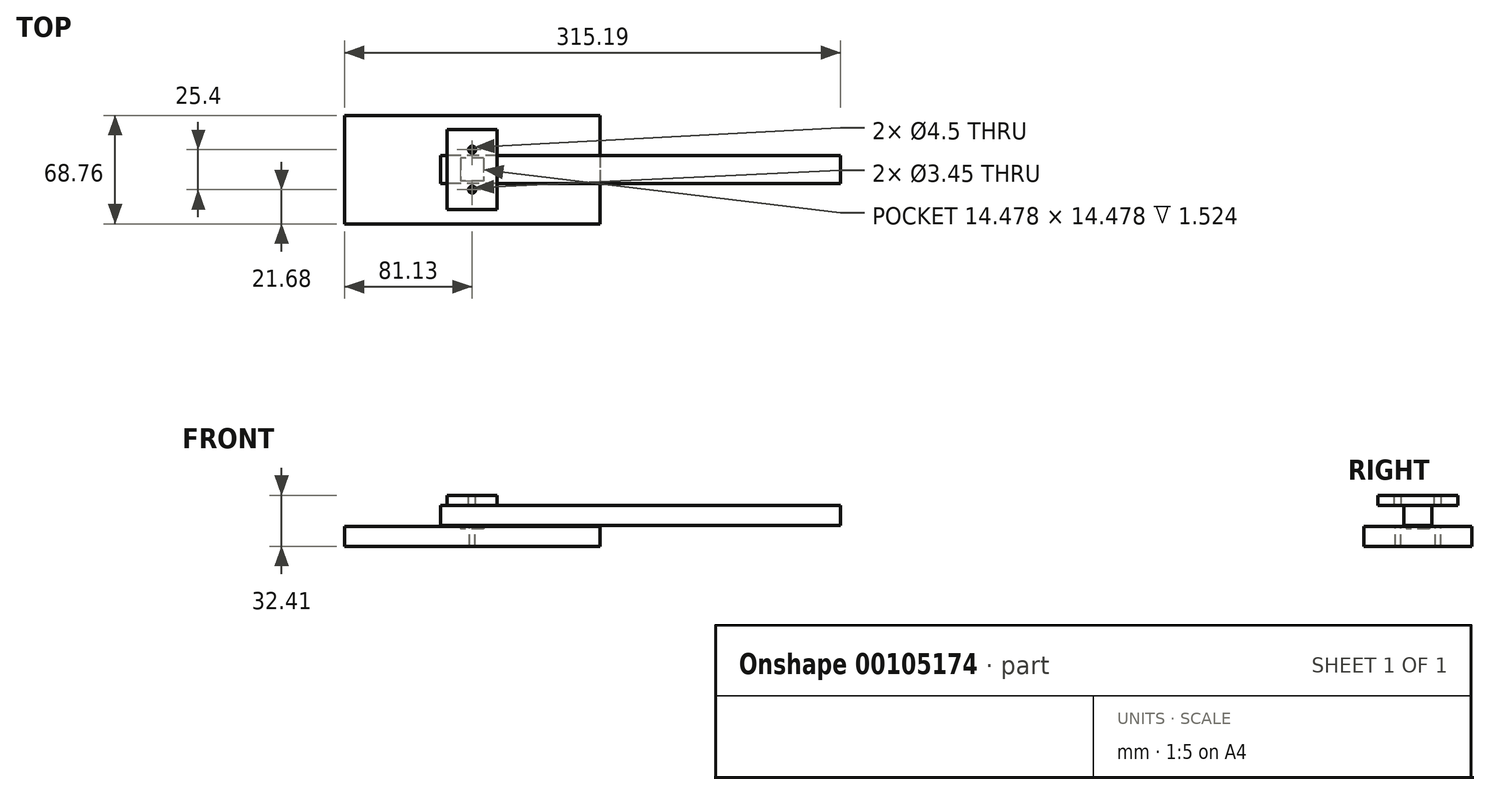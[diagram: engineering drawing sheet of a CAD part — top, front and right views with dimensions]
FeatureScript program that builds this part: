
annotation { "Feature Type Name" : "Feature", "Feature Type Description" : "" }
export const myFeature = defineFeature(function(context is Context, id is Id, definition is map)
    precondition{}
    {
        {
            var Q0;
            Q0=qCreatedBy(makeId("Top.planeOp"),FACE);
            var sketch = newSketch(context, id + "F0", { "sketchPlane" : qUnion([Q0])});
            skLineSegment(sketch, "E0.bottom", {"start": v(81.13, 34.38) * mm, "end": v(-81.13, 34.38) * mm});
            skLineSegment(sketch, "E0.top", {"start": v(81.13, -34.38) * mm, "end": v(-81.13, -34.38) * mm});
            skLineSegment(sketch, "E0.left", {"start": v(81.13, 34.38) * mm, "end": v(81.13, -34.38) * mm});
            skLineSegment(sketch, "E0.right", {"start": v(-81.13, 34.38) * mm, "end": v(-81.13, -34.38) * mm});
            skPoint(sketch, "E0.middle", {"position": v(0, 0) * mm});
            skSolve(sketch);
        }
        {
            var Q0;
            Q0=makeQuery(id+"F0.imprint","IMPRINT",FACE,{"disambiguationData":[TD([[makeQuery(id+"F0.imprint","IMPRINT",EDGE,{"derivedFrom":sQuery(id+"F0.wireOp",EDGE,"E0.bottom")}),1.0]])]});
            extrude(context, id + "F1", {"entities" : qUnion([Q0]), "depth" : 12.7 * mm});
        }
        {
            var Q0;
            Q0=makeQuery(id+"F1.opExtrude","CAP_FACE",FACE,{"disambiguationData":[OSD([sQuery(id+"F0.wireOp",EDGE,"E0.bottom"),sQuery(id+"F0.wireOp",EDGE,"E0.top"),sQuery(id+"F0.wireOp",EDGE,"E0.left"),sQuery(id+"F0.wireOp",EDGE,"E0.right")])],"isStart":false});
            var sketch = newSketch(context, id + "F2", { "sketchPlane" : qUnion([Q0])});
            skLineSegment(sketch, "E1.0.0", {"start": v(81.13, -34.38) * mm, "end": v(81.13, 34.38) * mm});
            skLineSegment(sketch, "E1.0.1", {"start": v(81.13, 34.38) * mm, "end": v(-81.13, 34.38) * mm});
            skLineSegment(sketch, "E1.0.2", {"start": v(-81.13, 34.38) * mm, "end": v(-81.13, -34.38) * mm});
            skLineSegment(sketch, "E1.0.3", {"start": v(-81.13, -34.38) * mm, "end": v(81.13, -34.38) * mm});
            skLineSegment(sketch, "E2", {"start": v(-81.13, 0) * mm, "end": v(81.13, 0) * mm, "construction": true});
            skLineSegment(sketch, "E3", {"start": v(0, 34.38) * mm, "end": v(0, -34.38) * mm, "construction": true});
            skLineSegment(sketch, "E4.bottom", {"start": v(7.24, 7.24) * mm, "end": v(-7.24, 7.24) * mm});
            skLineSegment(sketch, "E4.top", {"start": v(7.24, -7.24) * mm, "end": v(-7.24, -7.24) * mm});
            skLineSegment(sketch, "E4.left", {"start": v(7.24, 7.24) * mm, "end": v(7.24, -7.24) * mm});
            skLineSegment(sketch, "E4.right", {"start": v(-7.24, 7.24) * mm, "end": v(-7.24, -7.24) * mm});
            skPoint(sketch, "E4.middle", {"position": v(0, 0) * mm});
            skSolve(sketch);
        }
        {
            var Q0;
            Q0=makeQuery(id+"F2.imprint","IMPRINT",FACE,{"disambiguationData":[TD([[makeQuery(id+"F2.imprint","IMPRINT",EDGE,{"derivedFrom":sQuery(id+"F2.wireOp",EDGE,"E4.bottom")}),1.0]])]});
            extrude(context, id + "F3", {"entities" : qUnion([Q0]), "operationType" : NewBodyOperationType.REMOVE, "oppositeDirection" : true, "depth" : 1.52 * mm});
        }
        {
            var Q0;
            Q0=makeQuery(id+"F3.boolean.opBoolean","COPY",FACE,{"derivedFrom":makeQuery(id+"F3.opExtrude","CAP_FACE",FACE,{"disambiguationData":[OSD([sQuery(id+"F2.wireOp",EDGE,"E4.bottom"),sQuery(id+"F2.wireOp",EDGE,"E4.top"),sQuery(id+"F2.wireOp",EDGE,"E4.left"),sQuery(id+"F2.wireOp",EDGE,"E4.right")])],"isStart":false})});
            extrude(context, id + "F4", {"entities" : qUnion([Q0]), "depth" : 2.18 * mm});
        }
        {
            var Q0;
            Q0=makeQuery(id+"F4.opExtrude","SWEPT_FACE",FACE,{"disambiguationData":[OSD([sQuery(id+"F2.wireOp",EDGE,"E4.right")])]});
            cPlane(context, id + "F5", {"entities" : qUnion([Q0]), "cplaneType" : CPlaneType.OFFSET, "offset" : 12.7 * mm, "width" : 152.4 * mm, "height" : 152.4 * mm});
        }
        {
            var Q0;
            Q0=qCreatedBy(id+"F5.planeOp",FACE);
            var sketch = newSketch(context, id + "F6", { "sketchPlane" : qUnion([Q0])});
            skLineSegment(sketch, "E5.0.0", {"start": v(-7.24, 11.18) * mm, "end": v(7.24, 11.18) * mm});
            skLineSegment(sketch, "E5.0.1", {"start": v(7.24, 11.18) * mm, "end": v(7.24, 13.36) * mm});
            skLineSegment(sketch, "E5.0.2", {"start": v(7.24, 13.36) * mm, "end": v(-7.24, 13.36) * mm});
            skLineSegment(sketch, "E5.0.3", {"start": v(-7.24, 13.36) * mm, "end": v(-7.24, 11.18) * mm});
            skLineSegment(sketch, "E6.bottom", {"start": v(-8.9, 26.06) * mm, "end": v(8.89, 26.06) * mm});
            skLineSegment(sketch, "E6.top", {"start": v(-8.9, 13.36) * mm, "end": v(8.89, 13.36) * mm});
            skLineSegment(sketch, "E6.left", {"start": v(-8.9, 26.06) * mm, "end": v(-8.9, 13.36) * mm});
            skLineSegment(sketch, "E6.right", {"start": v(8.89, 26.06) * mm, "end": v(8.89, 13.36) * mm});
            skPoint(sketch, "E7", {"position": v(0, 13.36) * mm});
            skSolve(sketch);
        }
        {
            var Q0;
            Q0=makeQuery(id+"F6.imprint","IMPRINT",FACE,{"disambiguationData":[TD([[makeQuery(id+"F6.imprint","IMPRINT",EDGE,{"derivedFrom":sQuery(id+"F6.wireOp",EDGE,"E6.bottom")}),-1.0]])]});
            extrude(context, id + "F7", {"entities" : qUnion([Q0]), "oppositeDirection" : true, "depth" : 254 * mm});
        }
        {
            var Q0;
            Q0=makeQuery(id+"F7.opExtrude","SWEPT_FACE",FACE,{"disambiguationData":[OSD([sQuery(id+"F6.wireOp",EDGE,"E6.bottom")])]});
            var sketch = newSketch(context, id + "F8", { "sketchPlane" : qUnion([Q0])});
            skLineSegment(sketch, "E8.0.0", {"start": v(7.24, -7.24) * mm, "end": v(7.24, 7.24) * mm});
            skLineSegment(sketch, "E8.0.1", {"start": v(7.24, 7.24) * mm, "end": v(-7.24, 7.24) * mm});
            skLineSegment(sketch, "E8.0.2", {"start": v(-7.24, 7.24) * mm, "end": v(-7.24, -7.24) * mm});
            skLineSegment(sketch, "E8.0.3", {"start": v(-7.24, -7.24) * mm, "end": v(7.24, -7.24) * mm});
            skLineSegment(sketch, "E9.bottom", {"start": v(15.88, 25.4) * mm, "end": v(-15.87, 25.4) * mm});
            skLineSegment(sketch, "E9.top", {"start": v(15.88, -25.4) * mm, "end": v(-15.88, -25.4) * mm});
            skLineSegment(sketch, "E9.left", {"start": v(15.88, 25.4) * mm, "end": v(15.88, -25.4) * mm});
            skLineSegment(sketch, "E9.right", {"start": v(-15.87, 25.4) * mm, "end": v(-15.88, -25.4) * mm});
            skPoint(sketch, "E9.middle", {"position": v(0, 0) * mm});
            skSolve(sketch);
        }
        {
            var Q0;
            {var subQ0=sQuery(id+"F8.wireOp",EDGE,"E9.bottom");Q0=makeQuery(id+"F8.imprint","IMPRINT",FACE,{"disambiguationData":[TD([[makeQuery(id+"F8.imprint","IMPRINT",EDGE,{"derivedFrom":subQ0}),1.0]])]});}
            var Q1;
            Q1=makeQuery(id+"F8.imprint","IMPRINT",FACE,{"disambiguationData":[TD([[makeQuery(id+"F8.imprint","IMPRINT",EDGE,{"derivedFrom":sQuery(id+"F8.wireOp",EDGE,"E8.0.0")}),-1.0]])]});
            var Q2;
            {var subQ0=sQuery(id+"F8.wireOp",EDGE,"E9.top");Q2=makeQuery(id+"F8.imprint","IMPRINT",FACE,{"disambiguationData":[TD([[makeQuery(id+"F8.imprint","IMPRINT",EDGE,{"derivedFrom":subQ0}),-1.0]])]});}
            var Q3;
            Q3=makeQuery(id+"F8.imprint","IMPRINT",FACE,{"disambiguationData":[TD([[makeQuery(id+"F8.imprint","IMPRINT",EDGE,{"derivedFrom":sQuery(id+"F8.wireOp",EDGE,"E8.0.0")}),1.0]])]});
            extrude(context, id + "F9", {"entities" : qUnion([Q0, Q1, Q2, Q3]), "depth" : 6.35 * mm});
        }
        {
            var Q0;
            Q0=makeQuery(id+"F9.opExtrude","CAP_FACE",FACE,{"disambiguationData":[OSD([sQuery(id+"F8.wireOp",EDGE,"E8.0.0"),sQuery(id+"F8.wireOp",EDGE,"E8.0.1"),sQuery(id+"F8.wireOp",EDGE,"E8.0.2"),sQuery(id+"F8.wireOp",EDGE,"E8.0.3"),sQuery(id+"F8.wireOp",EDGE,"E9.bottom"),sQuery(id+"F8.wireOp",EDGE,"E9.top"),sQuery(id+"F8.wireOp",EDGE,"E9.left"),sQuery(id+"F8.wireOp",EDGE,"E9.right")])],"isStart":false});
            var sketch = newSketch(context, id + "F10", { "sketchPlane" : qUnion([Q0])});
            skLineSegment(sketch, "E10.0.0", {"start": v(15.88, -25.4) * mm, "end": v(15.88, 25.4) * mm});
            skLineSegment(sketch, "E10.0.1", {"start": v(15.88, 25.4) * mm, "end": v(-15.87, 25.4) * mm});
            skLineSegment(sketch, "E10.0.2", {"start": v(-15.87, 25.4) * mm, "end": v(-15.88, -25.4) * mm});
            skLineSegment(sketch, "E10.0.3", {"start": v(-15.88, -25.4) * mm, "end": v(15.88, -25.4) * mm});
            skLineSegment(sketch, "E11.0.0", {"start": v(7.24, -7.24) * mm, "end": v(7.24, 7.24) * mm});
            skLineSegment(sketch, "E11.0.1", {"start": v(7.24, 7.24) * mm, "end": v(-7.24, 7.24) * mm});
            skLineSegment(sketch, "E11.0.2", {"start": v(-7.24, 7.24) * mm, "end": v(-7.24, -7.24) * mm});
            skLineSegment(sketch, "E11.0.3", {"start": v(-7.24, -7.24) * mm, "end": v(7.24, -7.24) * mm});
            skLineSegment(sketch, "E12", {"start": v(0, 7.24) * mm, "end": v(0, 25.4) * mm, "construction": true});
            skLineSegment(sketch, "E13", {"start": v(0, -7.24) * mm, "end": v(0, -25.4) * mm, "construction": true});
            skPoint(sketch, "E14", {"position": v(0, -12.7) * mm});
            skLineSegment(sketch, "E15", {"start": v(-15.88, 0) * mm, "end": v(15.88, 0) * mm, "construction": true});
            skPoint(sketch, "E16.MirrorP", {"position": v(0, 12.7) * mm});
            skSolve(sketch);
        }
        {
            var Q0;
            Q0=sQuery(id+"F10.wireOp",VERTEX,"E16.MirrorP");
            var Q1;
            Q1=sQuery(id+"F10.wireOp",VERTEX,"E14");
            var Q2;
            Q2=makeQuery(id+"F9.opExtrude","SWEPT_BODY",BODY,{"disambiguationData":[OSD([sQuery(id+"F8.wireOp",EDGE,"E9.bottom"),sQuery(id+"F8.wireOp",EDGE,"E9.top"),sQuery(id+"F8.wireOp",EDGE,"E9.left"),sQuery(id+"F8.wireOp",EDGE,"E9.right")])]});
            var Q3;
            Q3=makeQuery(id+"F1.opExtrude","SWEPT_BODY",BODY,{"disambiguationData":[OSD([sQuery(id+"F0.wireOp",EDGE,"E0.bottom"),sQuery(id+"F0.wireOp",EDGE,"E0.top"),sQuery(id+"F0.wireOp",EDGE,"E0.left"),sQuery(id+"F0.wireOp",EDGE,"E0.right")])]});
            hole(context, id + "F11", {"style" : HoleStyle.SIMPLE, "endStyle" : HoleEndStyle.BLIND_IN_LAST, "standardTappedOrClearance" : lookupTablePath({ "fit" : "Normal", "standard" : "ANSI", "engagement" : "75%", "pitch" : "32 tpi", "size" : "#8", "type" : "Clearance & tapped" }), "standardBlindInLast" : lookupTablePath({ "standard" : "ANSI", "fit" : "Free", "engagement" : "75%", "pitch" : "32 tpi", "size" : "#8", "type" : "Clearance & tapped" }), "holeDiameter" : 4.5 * mm, "tapDrillDiameter" : 3.45 * mm, "holeDepth" : 15.24 * mm, "locations" : qUnion([Q0, Q1]), "scope" : qUnion([Q2, Q3]), "majorDiameter" : 4.17 * mm});
        }
    });
